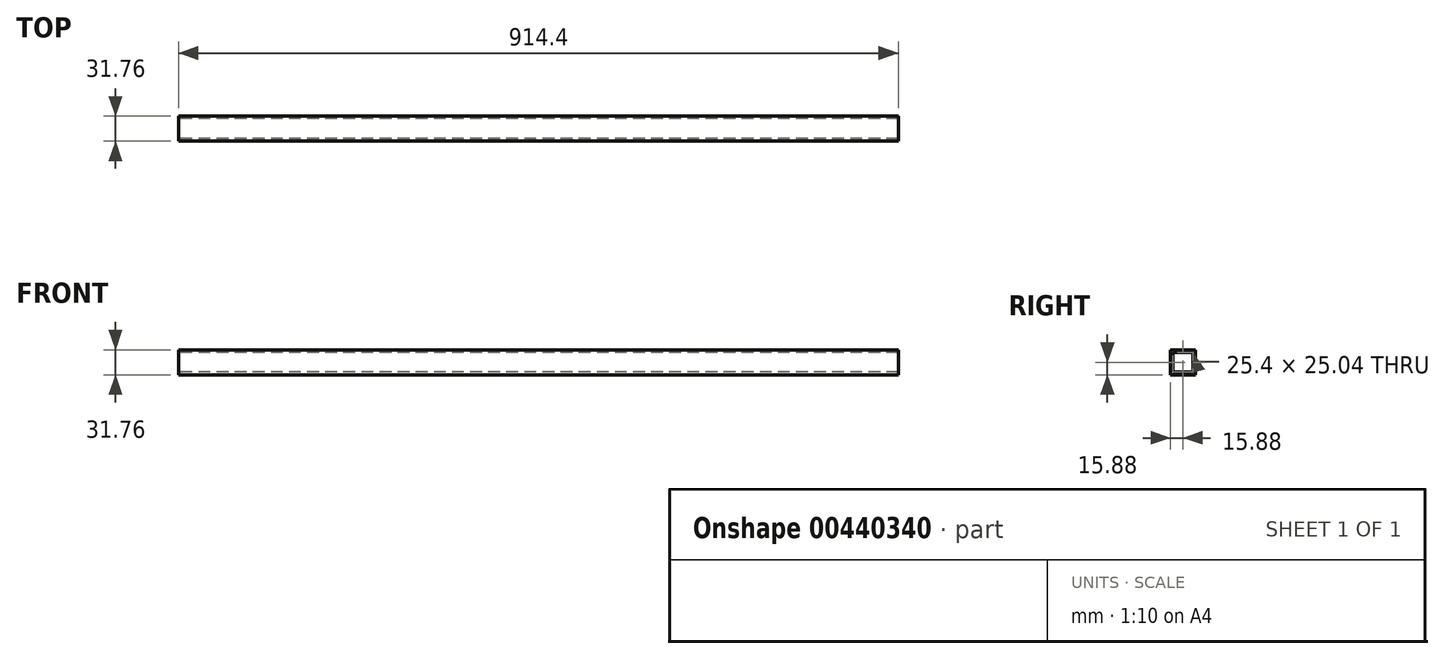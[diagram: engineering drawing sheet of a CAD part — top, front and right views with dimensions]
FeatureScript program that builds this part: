
annotation { "Feature Type Name" : "Feature", "Feature Type Description" : "" }
export const myFeature = defineFeature(function(context is Context, id is Id, definition is map)
    precondition{}
    {
        {
            var Q0;
            Q0=qCreatedBy(makeId("Front.planeOp"),FACE);
            var sketch = newSketch(context, id + "F0", { "sketchPlane" : qUnion([Q0])});
            skLineSegment(sketch, "E0.bottom", {"start": v(-457.2, 15.87) * mm, "end": v(457.2, 15.87) * mm});
            skLineSegment(sketch, "E0.top", {"start": v(-457.2, -15.87) * mm, "end": v(457.2, -15.87) * mm});
            skLineSegment(sketch, "E0.left", {"start": v(-457.2, 15.87) * mm, "end": v(-457.2, -15.87) * mm});
            skLineSegment(sketch, "E0.right", {"start": v(457.2, 15.87) * mm, "end": v(457.2, -15.87) * mm});
            skPoint(sketch, "E0.middle", {"position": v(0, 0) * mm});
            skSolve(sketch);
        }
        {
            var Q0;
            Q0=makeQuery(id+"F0.imprint","IMPRINT",FACE,{"disambiguationData":[TD([[makeQuery(id+"F0.imprint","IMPRINT",EDGE,{"derivedFrom":sQuery(id+"F0.wireOp",EDGE,"E0.bottom")}),-1.0]])]});
            extrude(context, id + "F1", {"entities" : qUnion([Q0]), "endBound" : BoundingType.SYMMETRIC, "depth" : 31.75 * mm});
        }
        {
            var Q0;
            Q0=makeQuery(id+"F1.opExtrude","SWEPT_FACE",FACE,{"disambiguationData":[OSD([sQuery(id+"F0.wireOp",EDGE,"E0.left")])]});
            var sketch = newSketch(context, id + "F2", { "sketchPlane" : qUnion([Q0])});
            skLineSegment(sketch, "E1.bottom", {"start": v(-12.7, 12.52) * mm, "end": v(12.7, 12.52) * mm});
            skLineSegment(sketch, "E1.top", {"start": v(-12.7, -12.52) * mm, "end": v(12.7, -12.52) * mm});
            skLineSegment(sketch, "E1.left", {"start": v(-12.7, 12.52) * mm, "end": v(-12.7, -12.52) * mm});
            skLineSegment(sketch, "E1.right", {"start": v(12.7, 12.52) * mm, "end": v(12.7, -12.52) * mm});
            skPoint(sketch, "E1.middle", {"position": v(0, 0) * mm});
            skSolve(sketch);
        }
        {
            var Q0;
            Q0=makeQuery(id+"F2.imprint","IMPRINT",FACE,{"disambiguationData":[TD([[makeQuery(id+"F2.imprint","IMPRINT",EDGE,{"derivedFrom":sQuery(id+"F2.wireOp",EDGE,"E1.bottom")}),-1.0]])]});
            extrude(context, id + "F3", {"entities" : qUnion([Q0]), "operationType" : NewBodyOperationType.REMOVE, "oppositeDirection" : true, "depth" : 914.4 * mm});
        }
    });
